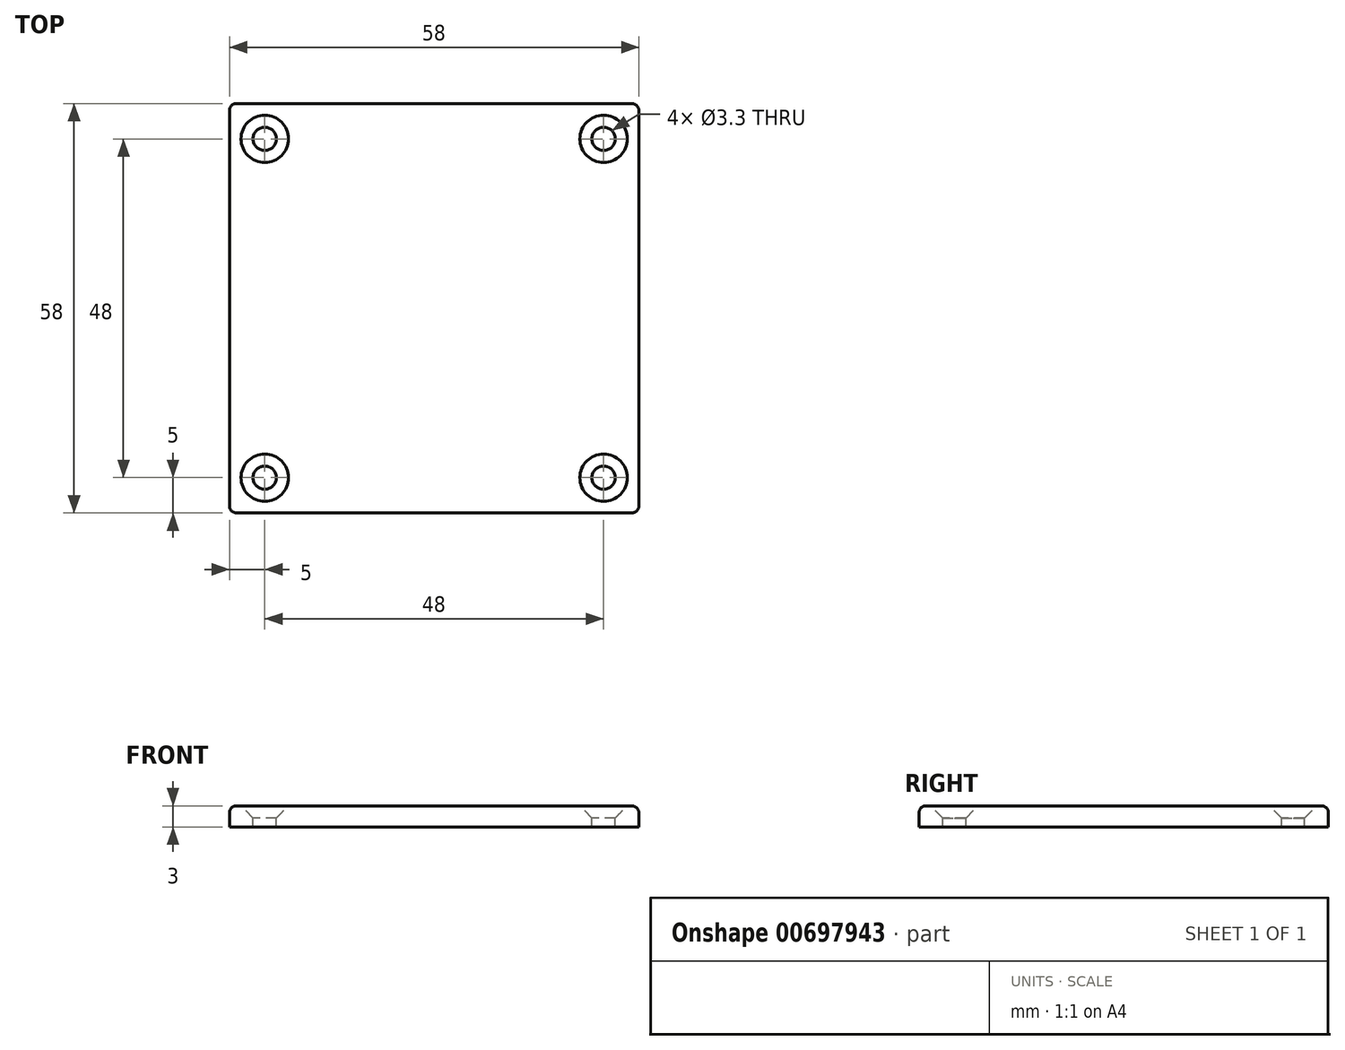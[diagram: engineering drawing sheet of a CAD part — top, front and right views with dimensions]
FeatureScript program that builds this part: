
annotation { "Feature Type Name" : "Feature", "Feature Type Description" : "" }
export const myFeature = defineFeature(function(context is Context, id is Id, definition is map)
    precondition{}
    {
        {
            var Q0;
            Q0=qCreatedBy(makeId("Top.planeOp"),FACE);
            var sketch = newSketch(context, id + "F0", { "sketchPlane" : qUnion([Q0])});
            skLineSegment(sketch, "E0.bottom", {"start": v(28, -29) * mm, "end": v(-28, -29) * mm});
            skLineSegment(sketch, "E0.top", {"start": v(28, 29) * mm, "end": v(-28, 29) * mm});
            skLineSegment(sketch, "E0.left", {"start": v(29, -28) * mm, "end": v(29, 28) * mm});
            skLineSegment(sketch, "E0.right", {"start": v(-29, -28) * mm, "end": v(-29, 28) * mm});
            skPoint(sketch, "E0.middle", {"position": v(0, 0) * mm});
            skPoint(sketch, "E1.visualSharp", {"position": v(-29, 29) * mm});
            skArc(sketch, "E1.filletArc", {"start": v(-28, 29) * mm, "mid": v(-28.7, 28.7) * mm, "end": v(-29, 28) * mm});
            skPoint(sketch, "E2.visualSharp", {"position": v(29, 29) * mm});
            skArc(sketch, "E2.filletArc", {"start": v(29, 28) * mm, "mid": v(28.7, 28.7) * mm, "end": v(28, 29) * mm});
            skPoint(sketch, "E3.visualSharp", {"position": v(29, -29) * mm});
            skArc(sketch, "E3.filletArc", {"start": v(28, -29) * mm, "mid": v(28.7, -28.7) * mm, "end": v(29, -28) * mm});
            skPoint(sketch, "E4.visualSharp", {"position": v(-29, -29) * mm});
            skArc(sketch, "E4.filletArc", {"start": v(-29, -28) * mm, "mid": v(-28.7, -28.7) * mm, "end": v(-28, -29) * mm});
            skSolve(sketch);
        }
        {
            var Q0;
            Q0=qSketchRegion(id+"F0",true);
            extrude(context, id + "F1", {"entities" : qUnion([Q0]), "depth" : 3 * mm, "offsetDistance" : 25 * mm});
        }
        {
            var Q0;
            Q0=makeQuery(id+"F1.opExtrude","CAP_EDGE",EDGE,{"disambiguationData":[OSD([sQuery(id+"F0.wireOp",EDGE,"E0.left")])],"isStart":false});
            fillet(context, id + "F2", {"entities" : qUnion([Q0]), "radius" : 1 * mm, "tangentPropagation" : true, "allowEdgeOverflow" : false});
        }
        {
            var Q0;
            Q0=makeQuery(id+"F1.opExtrude","CAP_FACE",FACE,{"disambiguationData":[OSD([sQuery(id+"F0.wireOp",EDGE,"E0.bottom"),sQuery(id+"F0.wireOp",EDGE,"E0.top"),sQuery(id+"F0.wireOp",EDGE,"E0.left"),sQuery(id+"F0.wireOp",EDGE,"E0.right"),sQuery(id+"F0.wireOp",EDGE,"E1.filletArc"),sQuery(id+"F0.wireOp",EDGE,"E2.filletArc"),sQuery(id+"F0.wireOp",EDGE,"E3.filletArc"),sQuery(id+"F0.wireOp",EDGE,"E4.filletArc")])],"isStart":false});
            var sketch = newSketch(context, id + "F3", { "sketchPlane" : qUnion([Q0])});
            skLineSegment(sketch, "E5.bottom", {"start": v(24, -24) * mm, "end": v(-24, -24) * mm, "construction": true});
            skLineSegment(sketch, "E5.top", {"start": v(24, 24) * mm, "end": v(-24, 24) * mm, "construction": true});
            skLineSegment(sketch, "E5.left", {"start": v(24, -24) * mm, "end": v(24, 24) * mm, "construction": true});
            skLineSegment(sketch, "E5.right", {"start": v(-24, -24) * mm, "end": v(-24, 24) * mm, "construction": true});
            skPoint(sketch, "E5.middle", {"position": v(0, 0) * mm});
            skPoint(sketch, "E6", {"position": v(-24, 24) * mm});
            skPoint(sketch, "E7", {"position": v(24, 24) * mm});
            skPoint(sketch, "E8", {"position": v(24, -24) * mm});
            skPoint(sketch, "E9", {"position": v(-24, -24) * mm});
            skSolve(sketch);
        }
        {
            var Q0;
            Q0=sQuery(id+"F3.wireOp",VERTEX,"E6");
            var Q1;
            Q1=sQuery(id+"F3.wireOp",VERTEX,"E7");
            var Q2;
            Q2=sQuery(id+"F3.wireOp",VERTEX,"E9");
            var Q3;
            Q3=sQuery(id+"F3.wireOp",VERTEX,"E8");
            var Q4;
            Q4=makeQuery(id+"F1.opExtrude","SWEPT_BODY",BODY,{"disambiguationData":[OSD([sQuery(id+"F0.wireOp",EDGE,"E0.bottom"),sQuery(id+"F0.wireOp",EDGE,"E0.top"),sQuery(id+"F0.wireOp",EDGE,"E0.left"),sQuery(id+"F0.wireOp",EDGE,"E0.right"),sQuery(id+"F0.wireOp",EDGE,"E1.filletArc"),sQuery(id+"F0.wireOp",EDGE,"E2.filletArc"),sQuery(id+"F0.wireOp",EDGE,"E3.filletArc"),sQuery(id+"F0.wireOp",EDGE,"E4.filletArc")])]});
            hole(context, id + "F4", {"style" : HoleStyle.C_SINK, "endStyle" : HoleEndStyle.THROUGH, "standardTappedOrClearance" : lookupTablePath({ "standard" : "ISO", "fit" : "Normal", "size" : "M3", "type" : "Clearance" }), "standardBlindInLast" : lookupTablePath({ "fit" : "Standard", "standard" : "ISO", "size" : "M3", "type" : "Clearance" }), "holeDiameter" : 3.3 * mm, "cSinkDiameter" : 6.72 * mm, "cSinkAngle" : 90 * degree, "majorDiameter" : 5 * mm, "tappedDepth" : 8 * mm, "tapClearance" : 3, "startFromSketch" : true, "locations" : qUnion([Q0, Q1, Q2, Q3]), "scope" : qUnion([Q4])});
        }
    });
